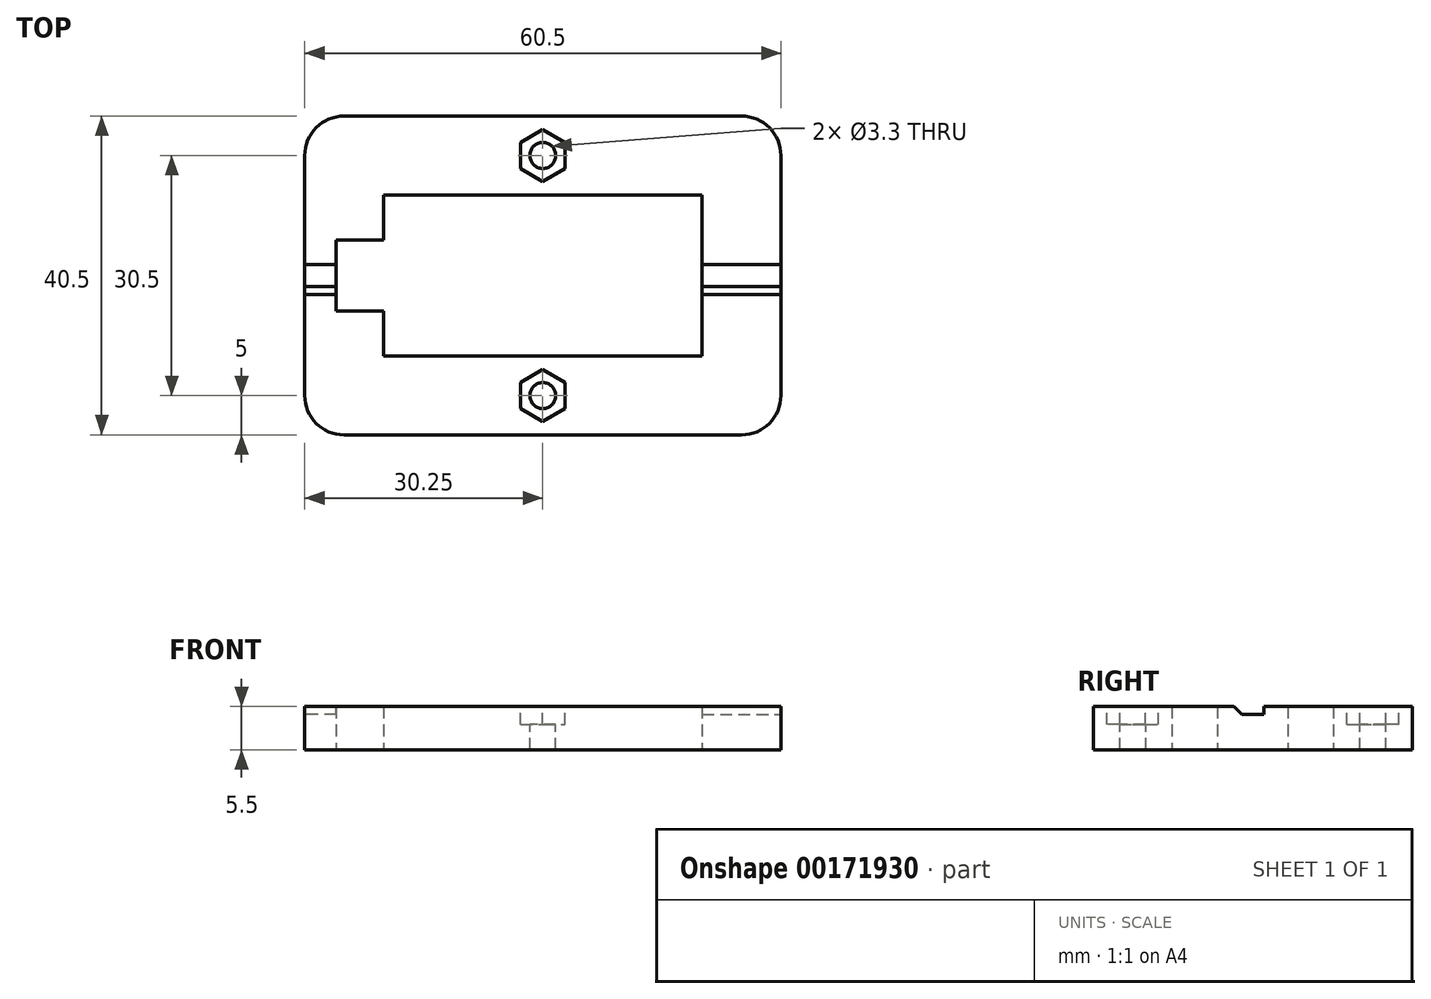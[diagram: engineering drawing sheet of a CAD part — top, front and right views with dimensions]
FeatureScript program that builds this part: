
annotation { "Feature Type Name" : "Feature", "Feature Type Description" : "" }
export const myFeature = defineFeature(function(context is Context, id is Id, definition is map)
    precondition{}
    {
        {
            var Q0;
            Q0=qCreatedBy(makeId("Top.planeOp"),FACE);
            var sketch = newSketch(context, id + "F0", { "sketchPlane" : qUnion([Q0])});
            skLineSegment(sketch, "E0.bottom", {"start": v(-20.25, 10.25) * mm, "end": v(20.25, 10.25) * mm});
            skLineSegment(sketch, "E0.top", {"start": v(-20.25, -10.25) * mm, "end": v(20.25, -10.25) * mm});
            skLineSegment(sketch, "E0.left", {"start": v(-20.25, 10.25) * mm, "end": v(-20.25, -10.25) * mm});
            skLineSegment(sketch, "E0.right", {"start": v(20.25, 10.25) * mm, "end": v(20.25, -10.25) * mm});
            skPoint(sketch, "E0.middle", {"position": v(0, 0) * mm});
            skLineSegment(sketch, "E1.0", {"start": v(-30.25, 20.25) * mm, "end": v(30.25, 20.25) * mm});
            skLineSegment(sketch, "E1.1", {"start": v(-30.25, 20.25) * mm, "end": v(-30.25, -20.25) * mm});
            skLineSegment(sketch, "E1.2", {"start": v(-30.25, -20.25) * mm, "end": v(30.25, -20.25) * mm});
            skLineSegment(sketch, "E1.3", {"start": v(30.25, 20.25) * mm, "end": v(30.25, -20.25) * mm});
            skLineSegment(sketch, "E2", {"start": v(25.25, 34.96) * mm, "end": v(25.25, -38.64) * mm, "construction": true});
            skSolve(sketch);
        }
        {
            var Q0;
            Q0=qSketchRegion(id+"F0",true);
            extrude(context, id + "F1", {"entities" : qUnion([Q0]), "depth" : 5.5 * mm});
        }
        {
            var Q0;
            Q0=makeQuery(id+"F1.opExtrude","CAP_FACE",FACE,{"disambiguationData":[OSD([sQuery(id+"F0.wireOp",EDGE,"E0.bottom"),sQuery(id+"F0.wireOp",EDGE,"E0.top"),sQuery(id+"F0.wireOp",EDGE,"E0.left"),sQuery(id+"F0.wireOp",EDGE,"E0.right"),sQuery(id+"F0.wireOp",EDGE,"E1.0"),sQuery(id+"F0.wireOp",EDGE,"E1.1"),sQuery(id+"F0.wireOp",EDGE,"E1.2"),sQuery(id+"F0.wireOp",EDGE,"E1.3")])],"isStart":false});
            var sketch = newSketch(context, id + "F2", { "sketchPlane" : qUnion([Q0])});
            skLineSegment(sketch, "E3", {"start": v(-20.25, 1.4) * mm, "end": v(-30.25, 1.4) * mm});
            skLineSegment(sketch, "E4.MirrorCS", {"start": v(-20.25, -1.4) * mm, "end": v(-30.25, -1.4) * mm});
            skLineSegment(sketch, "E5", {"start": v(20.25, 1.4) * mm, "end": v(30.25, 1.4) * mm});
            skLineSegment(sketch, "E6.MirrorCS", {"start": v(20.25, -1.4) * mm, "end": v(30.25, -1.4) * mm});
            skSolve(sketch);
        }
        {
            var Q0;
            {var subQ0=sQuery(id+"F2.wireOp",EDGE,"E3");Q0=makeQuery(id+"F2.imprint","IMPRINT",FACE,{"disambiguationData":[TD([[makeQuery(id+"F2.imprint","IMPRINT",EDGE,{"derivedFrom":subQ0}),1.0]])]});}
            var Q1;
            {var subQ0=sQuery(id+"F2.wireOp",EDGE,"E5");Q1=makeQuery(id+"F2.imprint","IMPRINT",FACE,{"disambiguationData":[TD([[makeQuery(id+"F2.imprint","IMPRINT",EDGE,{"derivedFrom":subQ0}),-1.0]])]});}
            extrude(context, id + "F3", {"entities" : qUnion([Q0, Q1]), "operationType" : NewBodyOperationType.REMOVE, "oppositeDirection" : true, "depth" : 1 * mm});
        }
        {
            var Q0;
            {var subQ0=sQuery(id+"F0.wireOp",EDGE,"E1.0");var subQ1=sQuery(id+"F0.wireOp",EDGE,"E0.left");var subQ2=sQuery(id+"F0.wireOp",EDGE,"E0.right");var subQ3=sQuery(id+"F0.wireOp",EDGE,"E0.bottom");var subQ4=sQuery(id+"F0.wireOp",EDGE,"E1.1");var subQ5=sQuery(id+"F0.wireOp",EDGE,"E1.3");Q0=makeQuery(id+"F3.boolean.opBoolean","SPLIT",FACE,{"disambiguationData":[TD([makeQuery(id+"F1.opExtrude","SWEPT_FACE",FACE,{"disambiguationData":[OSD([subQ3])]})])],"derivedFrom":makeQuery(id+"F1.opExtrude","CAP_FACE",FACE,{"disambiguationData":[OSD([subQ3,sQuery(id+"F0.wireOp",EDGE,"E0.top"),subQ1,subQ2,subQ0,subQ4,sQuery(id+"F0.wireOp",EDGE,"E1.2"),subQ5])],"isStart":false})});}
            var sketch = newSketch(context, id + "F4", { "sketchPlane" : qUnion([Q0])});
            skCircle(sketch, "E7", {"center": v(0, 15.25) * mm, "radius": 1.65 * mm});
            skPoint(sketch, "E7.centerSnap0", {"position": v(0, 20.25) * mm});
            skCircle(sketch, "E8.MirrorC", {"center": v(0, -15.25) * mm, "radius": 1.65 * mm});
            skSolve(sketch);
        }
        {
            var Q0;
            Q0=qSketchRegion(id+"F4",true);
            extrude(context, id + "F5", {"entities" : qUnion([Q0]), "operationType" : NewBodyOperationType.REMOVE, "oppositeDirection" : true, "depth" : 25 * mm});
        }
        {
            var Q0;
            Q0=makeQuery(id+"F1.opExtrude","CAP_FACE",FACE,{"disambiguationData":[OSD([sQuery(id+"F0.wireOp",EDGE,"E0.bottom"),sQuery(id+"F0.wireOp",EDGE,"E0.top"),sQuery(id+"F0.wireOp",EDGE,"E0.left"),sQuery(id+"F0.wireOp",EDGE,"E0.right"),sQuery(id+"F0.wireOp",EDGE,"E1.0"),sQuery(id+"F0.wireOp",EDGE,"E1.1"),sQuery(id+"F0.wireOp",EDGE,"E1.2"),sQuery(id+"F0.wireOp",EDGE,"E1.3")])],"isStart":true});
            var sketch = newSketch(context, id + "F6", { "sketchPlane" : qUnion([Q0])});
            skLineSegment(sketch, "E9.bottom", {"start": v(-20.25, 4.5) * mm, "end": v(-26.25, 4.5) * mm});
            skLineSegment(sketch, "E9.top", {"start": v(-20.25, -4.5) * mm, "end": v(-26.25, -4.5) * mm});
            skLineSegment(sketch, "E9.left", {"start": v(-20.25, 4.5) * mm, "end": v(-20.25, -4.5) * mm});
            skLineSegment(sketch, "E9.right", {"start": v(-26.25, 4.5) * mm, "end": v(-26.25, -4.5) * mm});
            skSolve(sketch);
        }
        {
            var Q0;
            Q0=qSketchRegion(id+"F6",true);
            extrude(context, id + "F7", {"entities" : qUnion([Q0]), "operationType" : NewBodyOperationType.REMOVE, "oppositeDirection" : true, "depth" : 25 * mm});
        }
        {
            var Q0;
            {var subQ0=sQuery(id+"F0.wireOp",EDGE,"E1.0");var subQ1=sQuery(id+"F0.wireOp",EDGE,"E0.left");var subQ2=sQuery(id+"F0.wireOp",EDGE,"E0.right");var subQ3=sQuery(id+"F0.wireOp",EDGE,"E0.bottom");var subQ4=sQuery(id+"F0.wireOp",EDGE,"E1.1");var subQ5=sQuery(id+"F0.wireOp",EDGE,"E1.3");Q0=makeQuery(id+"F3.boolean.opBoolean","SPLIT",FACE,{"disambiguationData":[TD([makeQuery(id+"F1.opExtrude","SWEPT_FACE",FACE,{"disambiguationData":[OSD([subQ3])]})])],"derivedFrom":makeQuery(id+"F1.opExtrude","CAP_FACE",FACE,{"disambiguationData":[OSD([subQ3,sQuery(id+"F0.wireOp",EDGE,"E0.top"),subQ1,subQ2,subQ0,subQ4,sQuery(id+"F0.wireOp",EDGE,"E1.2"),subQ5])],"isStart":false})});}
            var sketch = newSketch(context, id + "F8", { "sketchPlane" : qUnion([Q0])});
            skCircle(sketch, "E10.cCircle", {"center": v(0, 15.25) * mm, "radius": 2.85 * mm, "construction": true});
            skLineSegment(sketch, "E10.0", {"start": v(2.85, 16.9) * mm, "end": v(2.85, 13.6) * mm});
            skLineSegment(sketch, "E10.1", {"start": v(2.85, 13.6) * mm, "end": v(0, 11.96) * mm});
            skLineSegment(sketch, "E10.2", {"start": v(0, 11.96) * mm, "end": v(-2.85, 13.6) * mm});
            skLineSegment(sketch, "E10.3", {"start": v(-2.85, 13.6) * mm, "end": v(-2.85, 16.9) * mm});
            skLineSegment(sketch, "E10.4", {"start": v(-2.85, 16.9) * mm, "end": v(0, 18.54) * mm});
            skLineSegment(sketch, "E10.5", {"start": v(0, 18.54) * mm, "end": v(2.85, 16.9) * mm});
            skPoint(sketch, "E10.0.midPoint", {"position": v(2.85, 15.25) * mm});
            skLineSegment(sketch, "E11.MirrorCS", {"start": v(0, -18.54) * mm, "end": v(2.85, -16.9) * mm});
            skLineSegment(sketch, "E12.MirrorCS", {"start": v(-2.85, -16.9) * mm, "end": v(0, -18.54) * mm});
            skLineSegment(sketch, "E13.MirrorCS", {"start": v(-2.85, -13.6) * mm, "end": v(-2.85, -16.9) * mm});
            skLineSegment(sketch, "E14.MirrorCS", {"start": v(0, -11.96) * mm, "end": v(-2.85, -13.6) * mm});
            skLineSegment(sketch, "E15.MirrorCS", {"start": v(2.85, -13.6) * mm, "end": v(0, -11.96) * mm});
            skLineSegment(sketch, "E16.MirrorCS", {"start": v(2.85, -16.9) * mm, "end": v(2.85, -13.6) * mm});
            skCircle(sketch, "E17.MirrorC", {"center": v(0, -15.25) * mm, "radius": 2.85 * mm, "construction": true});
            skPoint(sketch, "E18.MirrorP", {"position": v(2.85, -15.25) * mm});
            skSolve(sketch);
        }
        {
            var Q0;
            Q0=qSketchRegion(id+"F8",true);
            extrude(context, id + "F9", {"entities" : qUnion([Q0]), "operationType" : NewBodyOperationType.REMOVE, "oppositeDirection" : true, "depth" : 2.3 * mm});
        }
        {
            var Q0;
            Q0=makeQuery(id+"F3.boolean.opBoolean","COPY",EDGE,{"derivedFrom":makeQuery(id+"F3.opExtrude","CAP_EDGE",EDGE,{"disambiguationData":[OSD([sQuery(id+"F2.wireOp",EDGE,"E5")])],"isStart":true})});
            var Q1;
            Q1=makeQuery(id+"F3.boolean.opBoolean","COPY",EDGE,{"derivedFrom":makeQuery(id+"F3.opExtrude","CAP_EDGE",EDGE,{"disambiguationData":[OSD([sQuery(id+"F2.wireOp",EDGE,"E6.MirrorCS")])],"isStart":true})});
            var Q2;
            Q2=makeQuery(id+"F3.boolean.opBoolean","COPY",EDGE,{"derivedFrom":makeQuery(id+"F3.opExtrude","CAP_EDGE",EDGE,{"disambiguationData":[OSD([sQuery(id+"F2.wireOp",EDGE,"E3")])],"isStart":true})});
            var Q3;
            Q3=makeQuery(id+"F3.boolean.opBoolean","COPY",EDGE,{"derivedFrom":makeQuery(id+"F3.opExtrude","CAP_EDGE",EDGE,{"disambiguationData":[OSD([sQuery(id+"F2.wireOp",EDGE,"E4.MirrorCS")])],"isStart":true})});
            chamfer(context, id + "F10", {"entities" : qUnion([Q0, Q1, Q2, Q3]), "width" : 1 * mm, "tangentPropagation" : true});
        }
        {
            var Q0;
            Q0=makeQuery(id+"F1.opExtrude","SWEPT_EDGE",EDGE,{"disambiguationData":[OSD([sQuery(id+"F0.wireOp",EDGE,"E1.0"),sQuery(id+"F0.wireOp",EDGE,"E1.3")])]});
            var Q1;
            Q1=makeQuery(id+"F1.opExtrude","SWEPT_EDGE",EDGE,{"disambiguationData":[OSD([sQuery(id+"F0.wireOp",EDGE,"E1.2"),sQuery(id+"F0.wireOp",EDGE,"E1.3")])]});
            var Q2;
            Q2=makeQuery(id+"F1.opExtrude","SWEPT_EDGE",EDGE,{"disambiguationData":[OSD([sQuery(id+"F0.wireOp",EDGE,"E1.1"),sQuery(id+"F0.wireOp",EDGE,"E1.2")])]});
            var Q3;
            Q3=makeQuery(id+"F1.opExtrude","SWEPT_EDGE",EDGE,{"disambiguationData":[OSD([sQuery(id+"F0.wireOp",EDGE,"E1.0"),sQuery(id+"F0.wireOp",EDGE,"E1.1")])]});
            fillet(context, id + "F11", {"entities" : qUnion([Q0, Q1, Q2, Q3]), "radius" : 5 * mm, "tangentPropagation" : true, "allowEdgeOverflow" : false});
        }
    });
